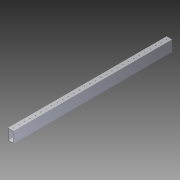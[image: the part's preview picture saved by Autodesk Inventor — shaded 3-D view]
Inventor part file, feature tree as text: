
AUTODESK INVENTOR PART (.ipt)
format: ipt  version: 2014 SP1 (Build 180222100, 222)  size: 724,992 bytes
history: native  units: in
note: dims shown in document units (in); Inventor stores cm internally (conversion verified against a paired STEP export)
features: other x2, extrude x1, imported_body x1, sketch x1
ambient origin geometry x8: Origin, YZ Plane, XZ Plane, XY Plane, X Axis, Y Axis, Z Axis, Center Point
bodies: Body1 (feature_tree)
feature tree (5):
  other  "Cut-Extrude2"
  other  "2x1 Tube1"
  extrude  "Extrusion1"  [1 undecoded]
  imported_body  "Base1"
  sketch  "Sketch1"  dims[d0=30.0in d1=0.0in]
note: 1 required parameter value undecoded (feature->parameter linkage not recoverable at this tier; creation-order binding heuristic only, values carry confidence <= 0.55)
